# Revit family: Mark IV Horizontal - Bi-Parting (Power)
name_source: partatom
category: Doors
revit_build: Autodesk Revit 2014 (Build: 20140709_2115(x64)
units: mm (PartAtom-declared; Revit-internal decimal feet)

## types (5) — shared parameters
Analytic Construction = <None>
Closure Offset = 8"
DOOR CLOSER = 14"
Frame = <By Category>
Frame Projection Ext. = 1"
Frame Projection Int. = 1"
Frame Width = 3"
Function = Interior
LATCH STRIKE TAPPING BAR = 41"
Shutter = <By Category>
Wall Closure = By host

## per-type parameters (varying)
| type | Clearance Required | HIC | Height | OVERALL FRAME HEIGHT | OVERALL FRAME WIDTH | WIC | Width |
| 3'-0" X 6'-8" | 99" | 77 1/2" | 60" | 79 1/2" | 44" | 40" | 36" |
| MARK IV Horizontal Bi parting (Power) | 141" | 90" | 60" | 92" | 65" | 61" | 36" |
| 3'-0" X 8'-0" | 91" | 96" | 96" | 98" | 40" | 36" | 36" |
| 4'-0" X 7'-0" | 115" | 84" | 84" | 86" | 52" | 48" | 48" |
| 4'-0" X 8'-0" | 115" | 96" | 96" | 98" | 52" | 48" | 48" |

## geometry (parser evidence)
native form markers: Sweep x8
no freeform markers — native parametric forms only
